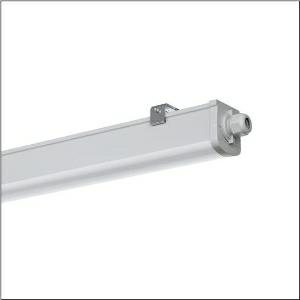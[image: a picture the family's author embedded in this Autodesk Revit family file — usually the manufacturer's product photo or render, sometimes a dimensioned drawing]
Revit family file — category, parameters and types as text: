
# Revit family: monsun_r__31_51fa207k430b_6f38
name_source: partatom
category: Lighting Fixtures
units: mm (PartAtom-declared; Revit-internal decimal feet)

## family parameters
Cut with Voids When Loaded = No
Host = Face
Light Source = No
Part Type = Normal
Room Calculation Point = No
Round Connector Dimension = Use Diameter
Shared = No

## types (1)
- Monsun® 31 (1 x LED, 3000 lm, 22 W, 4000K)
    Apparent Load = 22 VA
    CIE Flux Codes = 42 72 91 92 100
    Color Rendering = 80
    Color Temperature = 4000K
    Default Elevation = 1800 mm
    Description = Monsun® 31, damp-proof luminaire, primary optical cover: diffuser, of PC, frosted, light emission: direct distribution, primary light characteristic: symmetric, installation type: surface-mounted, LED, rated luminous flux: 3.000lm, luminous efficacy: 136lm/W, light colour: 840, colour temperature: 4000K, control gear: ECG, with terminal, 3+1-pole, max. 2.5mm², through-wiring: 3x 2.5mm² + 1x 1.5mm², mains connection: 220..240V, AC, 50/60Hz, rated input power: 22W, housing, luminaire housing, of PC, light grey (RAL 7035), length: 1.158mm, width: 68mm, height: 76mm, protection rating (complete): IP66, insulation class (complete): insulation class II (safety insulation), certification: CE, ENEC, UKCA, protection symbol: D, impact resistance: IK08, permissible operating ambient temperature: -20..+40°C, corresponds to IFS (International Featured Standards) requirements for safety and quality in the food industry, packaging unit: 1 piece
    Height = 77 mm
    Lamp = 1 x LED
    Lamp Light Flux = 3000 lm
    Lamp Power = 22 W
    Lamp count = 1
    Length = 1218 mm
    Luminous efficacy = 136 lm/W
    Manufacturer = Siteco
    ModVariant = No
    Model = 51FA207K430B
    Mounting Place = Ceiling
    Mounting Type = Surface mounted
    Number of Poles = 1
    OnlyDefault = Yes
    Power Factor = 1
    Product Name = Monsun® 31
    Product group = damp-proof luminaire | ceiling mounted
    ProductGroupID = 300
    Protection Class = Protection class II
    Protection Degree = IP 66
    RLX_Detail_Level = 1
    RlxData = <blob elided: 32749 chars, md5=20f84bcd>
    Socket = socket
    Standby Power = 0 W
    System Light Flux = 3000 lm
    System Power = 22 W
    Type Comments = Product without accessories
    Type Image = l_1006174.jpg
    URL = http://relux.com
    VarID = ---
    Voltage = 0 V
    Weight = 0.00 kg
    Width = 69 mm

## geometry (parser evidence)
native form markers: Blend x4, Sweep x12
no freeform markers — native parametric forms only
